# Revit family: Haworth_Planes_InformationDisplay_AP_PRELIMINARY
name_source: partatom
category: Furniture Systems
units: mm (PartAtom-declared; Revit-internal decimal feet)

## family parameters
Always vertical = Yes
Cut with Voids When Loaded = No
OmniClass Number = 23.40.70.14.64.21
OmniClass Title = Systems Furniture
Part Type = Normal
Room Calculation Point = No
Round Connector Dimension = Use Diameter
Shared = No
Work Plane-Based = No

## types (2) — shared parameters
Actual Height = 1905 mm  [stored 6.25 ft]
Assembly Code = E2020200
Caster Finish = Haworth _ Polymer _ Black
Description = Haworth - Planes - Information Display
Hook Finish = Haworth _ Polymer _ Undecided
Manufacturer = Haworth
Model = WOPLID
Revision Number = 1
Size = Verify Final Dim. w/ Haworth
URL = www.haworth.com
URL - Product = http://www.haworth.com
Warranty = http://www.haworth.com

## per-type parameters (varying)
| type | Actual Width | Casters | Glides | Large |
| Standard | 1143 mm  [stored 3.75 ft] | No | Yes | No |
| Large | 2235 mm  [stored 7.33268 ft] | Yes | No | Yes |

note: [stored X ft] marks values corroborated as IEEE doubles in the binary element streams (Revit-internal decimal feet)

## geometry (parser evidence)
native form markers: Blend x2, Sweep x10
no freeform markers — native parametric forms only
